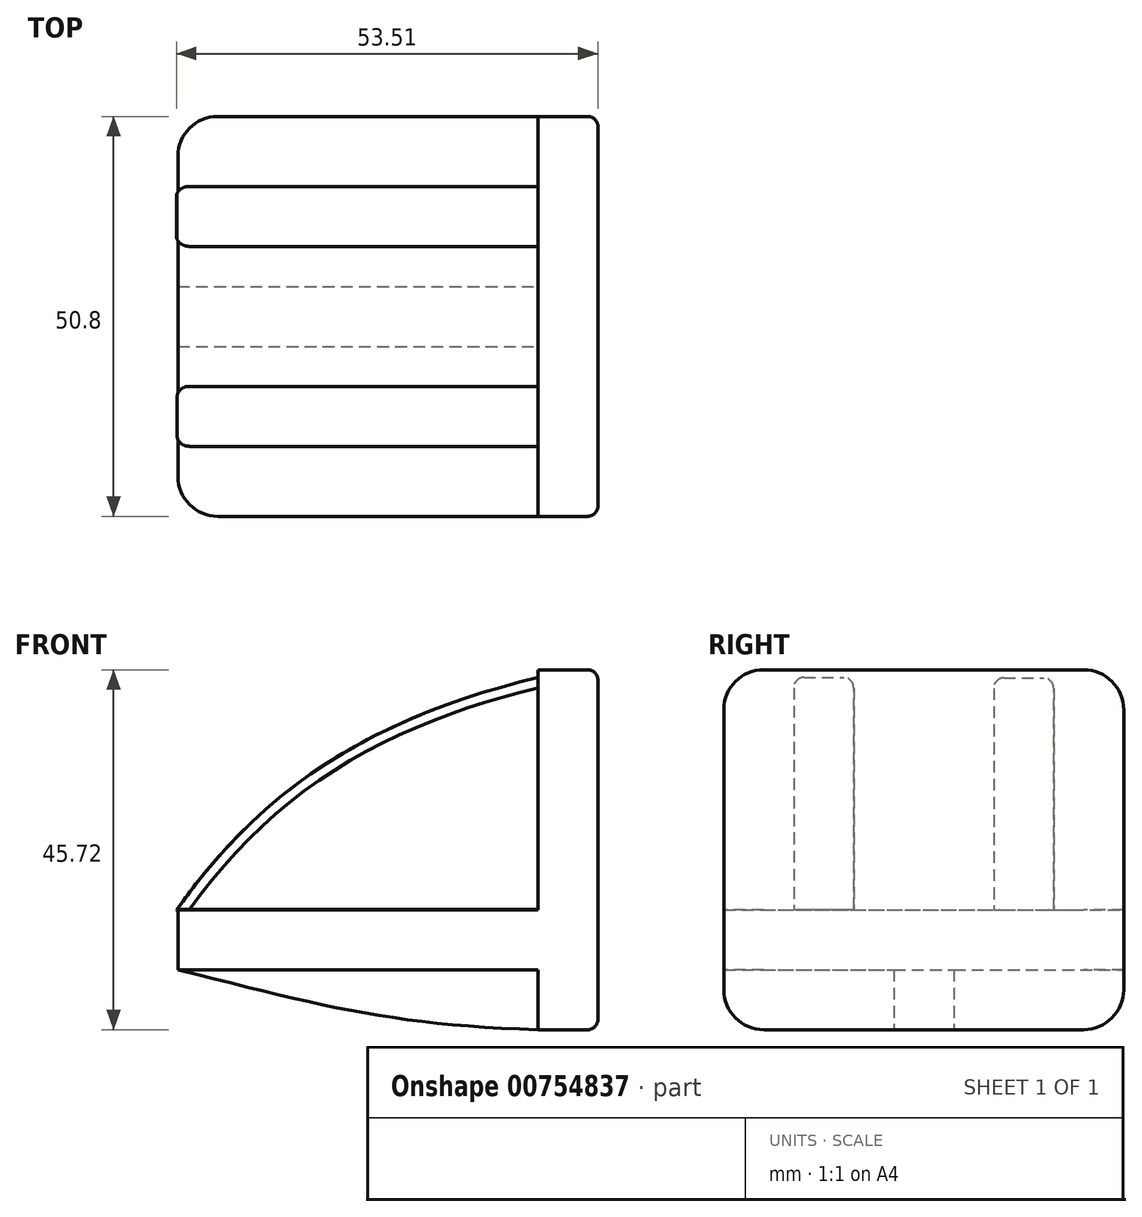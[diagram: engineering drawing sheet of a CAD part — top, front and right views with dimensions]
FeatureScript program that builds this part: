
annotation { "Feature Type Name" : "Feature", "Feature Type Description" : "" }
export const myFeature = defineFeature(function(context is Context, id is Id, definition is map)
    precondition{}
    {
        {
            var Q0;
            Q0=qCreatedBy(makeId("Front.planeOp"),FACE);
            var sketch = newSketch(context, id + "F0", { "sketchPlane" : qUnion([Q0])});
            skLineSegment(sketch, "E0.bottom", {"start": v(18.94, 38.1) * mm, "end": v(26.56, 38.1) * mm});
            skLineSegment(sketch, "E0.top", {"start": v(18.94, -7.62) * mm, "end": v(26.56, -7.62) * mm});
            skLineSegment(sketch, "E0.left", {"start": v(18.94, 38.1) * mm, "end": v(18.94, -7.62) * mm});
            skLineSegment(sketch, "E0.right", {"start": v(26.56, 38.1) * mm, "end": v(26.56, -7.62) * mm});
            skLineSegment(sketch, "E1.bottom", {"start": v(-26.78, 7.62) * mm, "end": v(18.94, 7.62) * mm});
            skLineSegment(sketch, "E1.top", {"start": v(-26.78, 0) * mm, "end": v(18.94, 0) * mm});
            skLineSegment(sketch, "E1.left", {"start": v(-26.78, 7.62) * mm, "end": v(-26.78, 0) * mm});
            skLineSegment(sketch, "E1.right", {"start": v(18.94, 7.62) * mm, "end": v(18.94, 0) * mm});
            skFitSpline(sketch, "E2", {"points": [v(-26.78, 0) * mm, v(18.94, -7.62) * mm], "startDerivative": vector(55, -13.9) * mm, "endDerivative": vector(55.01, -1.68) * mm});
            skSolve(sketch);
        }
        {
            var Q0;
            Q0=makeQuery(id+"F0.imprint","IMPRINT",FACE,{"disambiguationData":[TD([[makeQuery(id+"F0.imprint","IMPRINT",EDGE,{"derivedFrom":sQuery(id+"F0.wireOp",EDGE,"E1.bottom")}),-1.0]])]});
            extrude(context, id + "F1", {"entities" : qUnion([Q0]), "endBound" : BoundingType.SYMMETRIC, "depth" : 50.8 * mm, "offsetDistance" : 25.4 * mm});
        }
        {
            var Q0;
            {var subQ3=sQuery(id+"F0.wireOp",EDGE,"E0.bottom");Q0=makeQuery(id+"F0.imprint","IMPRINT",FACE,{"disambiguationData":[TD([[makeQuery(id+"F0.imprint","IMPRINT",EDGE,{"derivedFrom":subQ3}),-1.0]])]});}
            extrude(context, id + "F2", {"entities" : qUnion([Q0]), "operationType" : NewBodyOperationType.ADD, "endBound" : BoundingType.SYMMETRIC, "depth" : 50.8 * mm, "offsetDistance" : 25.4 * mm});
        }
        {
            var Q0;
            {var subQ2=sQuery(id+"F0.wireOp",EDGE,"E1.top");Q0=makeQuery(id+"F0.imprint","IMPRINT",FACE,{"disambiguationData":[TD([[makeQuery(id+"F0.imprint","IMPRINT",EDGE,{"derivedFrom":subQ2}),-1.0]])]});}
            extrude(context, id + "F3", {"entities" : qUnion([Q0]), "operationType" : NewBodyOperationType.ADD, "endBound" : BoundingType.SYMMETRIC, "depth" : 7.62 * mm, "offsetDistance" : 25.4 * mm});
        }
        {
            var Q0;
            Q0=makeQuery(id+"F2.opExtrude","CAP_EDGE",EDGE,{"disambiguationData":[OSD([sQuery(id+"F0.wireOp",EDGE,"E0.top")])],"isStart":false});
            var Q1;
            Q1=makeQuery(id+"F2.opExtrude","CAP_EDGE",EDGE,{"disambiguationData":[OSD([sQuery(id+"F0.wireOp",EDGE,"E0.top")])],"isStart":true});
            var Q2;
            Q2=makeQuery(id+"F2.opExtrude","CAP_EDGE",EDGE,{"disambiguationData":[OSD([sQuery(id+"F0.wireOp",EDGE,"E0.bottom")])],"isStart":true});
            var Q3;
            Q3=makeQuery(id+"F2.opExtrude","CAP_EDGE",EDGE,{"disambiguationData":[OSD([sQuery(id+"F0.wireOp",EDGE,"E0.bottom")])],"isStart":false});
            var Q4;
            Q4=makeQuery(id+"F1.opExtrude","CAP_EDGE",EDGE,{"disambiguationData":[OSD([sQuery(id+"F0.wireOp",EDGE,"E1.left")])],"isStart":true});
            var Q5;
            Q5=makeQuery(id+"F1.opExtrude","CAP_EDGE",EDGE,{"disambiguationData":[OSD([sQuery(id+"F0.wireOp",EDGE,"E1.left")])],"isStart":false});
            fillet(context, id + "F4", {"entities" : qUnion([Q0, Q1, Q2, Q3, Q4, Q5]), "radius" : 5.08 * mm, "tangentPropagation" : true, "allowEdgeOverflow" : false});
        }
        {
            var Q0;
            Q0=qCreatedBy(makeId("Front.planeOp"),FACE);
            cPlane(context, id + "F5", {"entities" : qUnion([Q0]), "cplaneType" : CPlaneType.OFFSET, "offset" : 12.7 * mm, "width" : 152.4 * mm, "height" : 152.4 * mm});
        }
        {
            var Q0;
            Q0=qCreatedBy(id+"F5.planeOp",FACE);
            var sketch = newSketch(context, id + "F6", { "sketchPlane" : qUnion([Q0])});
            skFitSpline(sketch, "E3", {"points": [v(19.5, 37.26) * mm, v(-26.86, 7.68) * mm], "startDerivative": vector(-65.32, -15.62) * mm, "endDerivative": vector(-32.66, -46.15) * mm});
            skLineSegment(sketch, "E4", {"start": v(19.5, 37.26) * mm, "end": v(19.5, 7.64) * mm});
            skLineSegment(sketch, "E5", {"start": v(19.5, 7.64) * mm, "end": v(-26.86, 7.68) * mm});
            skSolve(sketch);
        }
        {
            var Q0;
            Q0 = qSketchRegion(id + "F6", true);
            extrude(context, id + "F7", {"entities" : qUnion([Q0]), "operationType" : NewBodyOperationType.ADD, "endBound" : BoundingType.SYMMETRIC, "depth" : 7.62 * mm, "offsetDistance" : 25.4 * mm});
        }
        {
            var Q0;
            Q0=qCreatedBy(makeId("Front.planeOp"),FACE);
            cPlane(context, id + "F8", {"entities" : qUnion([Q0]), "cplaneType" : CPlaneType.OFFSET, "offset" : 12.7 * mm, "oppositeDirection" : true, "width" : 152.4 * mm, "height" : 152.4 * mm});
        }
        {
            var Q0;
            Q0=qCreatedBy(id+"F8.planeOp",FACE);
            var sketch = newSketch(context, id + "F9", { "sketchPlane" : qUnion([Q0])});
            skFitSpline(sketch, "E6", {"points": [v(19.42, 37.17) * mm, v(-26.95, 7.6) * mm], "startDerivative": vector(-65.32, -15.62) * mm, "endDerivative": vector(-32.66, -46.15) * mm});
            skLineSegment(sketch, "E7", {"start": v(19.42, 37.17) * mm, "end": v(19.42, 7.56) * mm});
            skLineSegment(sketch, "E8", {"start": v(19.42, 7.56) * mm, "end": v(-26.95, 7.6) * mm});
            skSolve(sketch);
        }
        {
            var Q0;
            Q0=makeQuery(id+"F9.imprint","IMPRINT",FACE,{"disambiguationData":[TD([[makeQuery(id+"F9.imprint","IMPRINT",EDGE,{"derivedFrom":sQuery(id+"F9.wireOp",EDGE,"E6")}),1.0]])]});
            extrude(context, id + "F10", {"entities" : qUnion([Q0]), "operationType" : NewBodyOperationType.ADD, "endBound" : BoundingType.SYMMETRIC, "depth" : 7.62 * mm, "offsetDistance" : 25.4 * mm});
        }
        {
            var Q0;
            Q0=makeQuery(id+"F2.opExtrude","SWEPT_FACE",FACE,{"disambiguationData":[OSD([sQuery(id+"F0.wireOp",EDGE,"E0.right")])]});
            var Q1;
            Q1=makeQuery(id+"F7.opExtrude","CAP_EDGE",EDGE,{"disambiguationData":[OSD([sQuery(id+"F6.wireOp",EDGE,"E3")])],"isStart":false});
            var Q2;
            Q2=makeQuery(id+"F7.opExtrude","CAP_EDGE",EDGE,{"disambiguationData":[OSD([sQuery(id+"F6.wireOp",EDGE,"E3")])],"isStart":true});
            var Q3;
            Q3=makeQuery(id+"F10.opExtrude","CAP_EDGE",EDGE,{"disambiguationData":[OSD([sQuery(id+"F9.wireOp",EDGE,"E6")])],"isStart":true});
            var Q4;
            Q4=makeQuery(id+"F10.opExtrude","CAP_EDGE",EDGE,{"disambiguationData":[OSD([sQuery(id+"F9.wireOp",EDGE,"E6")])],"isStart":false});
            fillet(context, id + "F11", {"entities" : qUnion([Q0, Q1, Q2, Q3, Q4]), "radius" : 1.27 * mm, "tangentPropagation" : true, "allowEdgeOverflow" : false});
        }
    });
